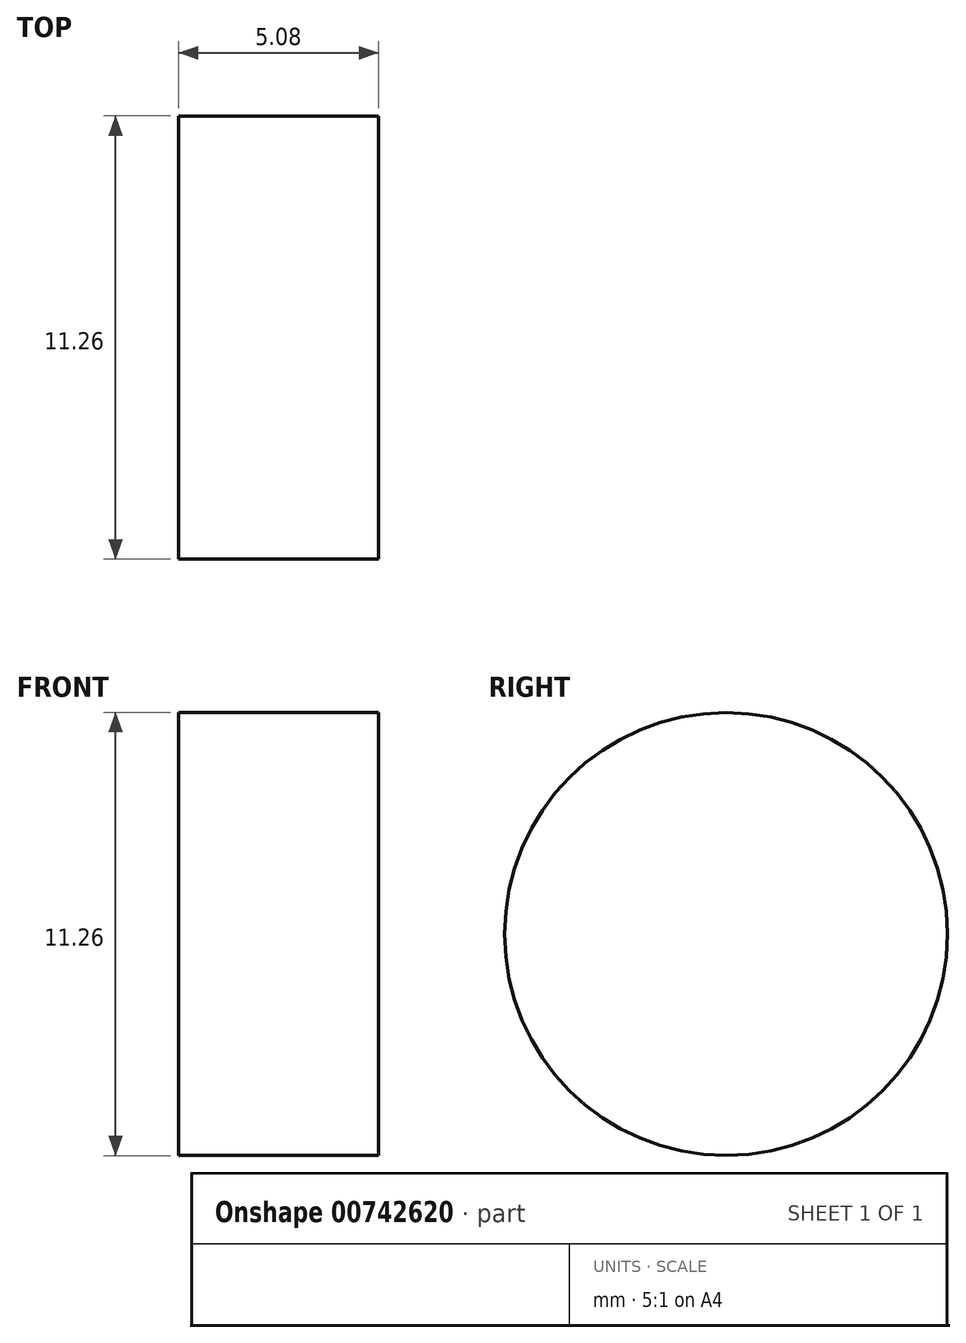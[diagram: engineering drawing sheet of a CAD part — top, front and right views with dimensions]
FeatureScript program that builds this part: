
annotation { "Feature Type Name" : "Feature", "Feature Type Description" : "" }
export const myFeature = defineFeature(function(context is Context, id is Id, definition is map)
    precondition{}
    {
        {
            var Q0;
            Q0=qCreatedBy(makeId("Right.planeOp"),FACE);
            var sketch = newSketch(context, id + "F0", { "sketchPlane" : qUnion([Q0])});
            skCircle(sketch, "E0", {"center": v(0, 0) * mm, "radius": 5.63 * mm});
            skSolve(sketch);
        }
        {
            var Q0;
            Q0 = qSketchRegion(id + "F0", true);
            extrude(context, id + "F1", {"entities" : qUnion([Q0]), "depth" : 5.08 * mm, "offsetDistance" : 25.4 * mm});
        }
    });
